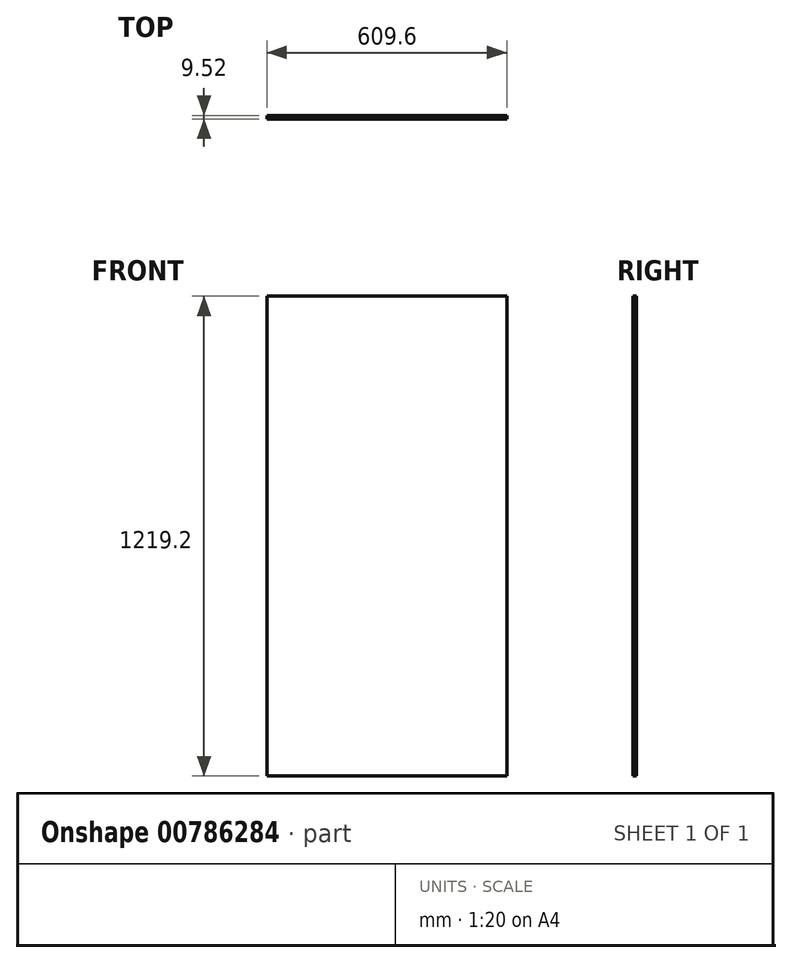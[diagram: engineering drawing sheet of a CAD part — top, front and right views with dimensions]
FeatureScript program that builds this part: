
annotation { "Feature Type Name" : "Feature", "Feature Type Description" : "" }
export const myFeature = defineFeature(function(context is Context, id is Id, definition is map)
    precondition{}
    {
        {
            var Q0;
            Q0=qCreatedBy(makeId("Front.planeOp"),FACE);
            var sketch = newSketch(context, id + "F0", { "sketchPlane" : qUnion([Q0])});
            skLineSegment(sketch, "E0.bottom", {"start": v(-304.8, 609.6) * mm, "end": v(304.8, 609.6) * mm});
            skLineSegment(sketch, "E0.top", {"start": v(-304.8, -609.6) * mm, "end": v(304.8, -609.6) * mm});
            skLineSegment(sketch, "E0.left", {"start": v(-304.8, 609.6) * mm, "end": v(-304.8, -609.6) * mm});
            skLineSegment(sketch, "E0.right", {"start": v(304.8, 609.6) * mm, "end": v(304.8, -609.6) * mm});
            skPoint(sketch, "E0.middle", {"position": v(0, 0) * mm});
            skSolve(sketch);
        }
        {
            var Q0;
            Q0=makeQuery(id+"F0.imprint","IMPRINT",FACE,{"disambiguationData":[TD([[makeQuery(id+"F0.imprint","IMPRINT",EDGE,{"derivedFrom":sQuery(id+"F0.wireOp",EDGE,"E0.bottom")}),-1.0]])]});
            extrude(context, id + "F1", {"entities" : qUnion([Q0]), "endBound" : BoundingType.SYMMETRIC, "depth" : 9.52 * mm, "offsetDistance" : 25.4 * mm});
        }
    });
